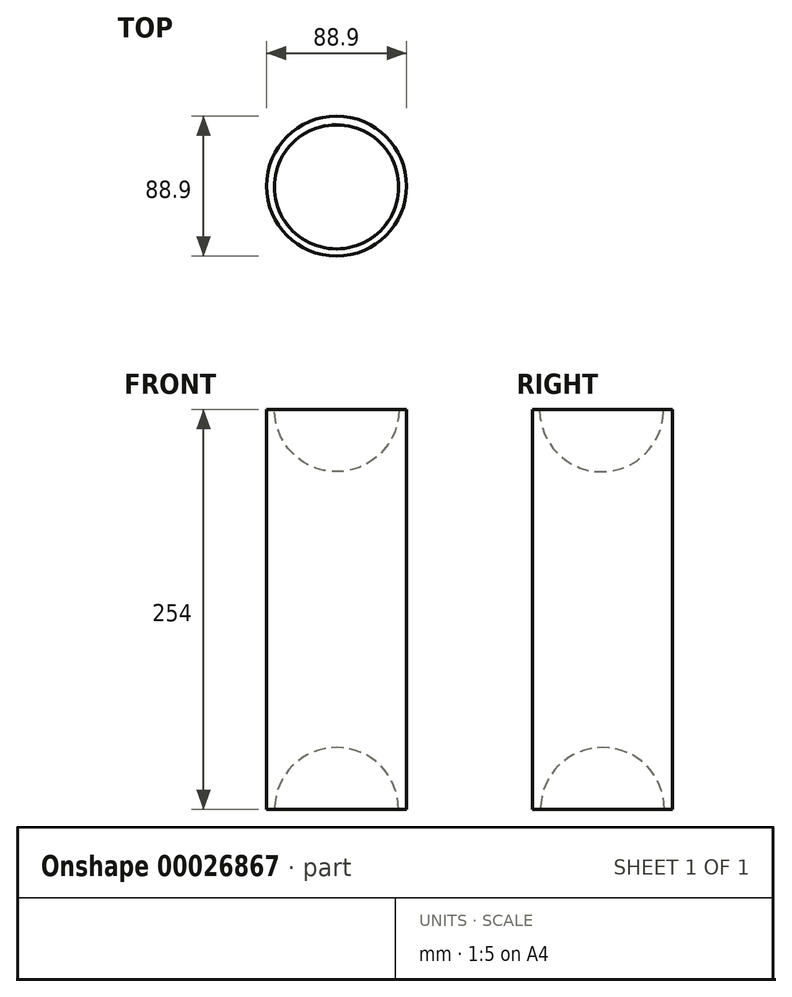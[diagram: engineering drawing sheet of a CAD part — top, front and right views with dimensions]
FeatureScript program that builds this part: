
annotation { "Feature Type Name" : "Feature", "Feature Type Description" : "" }
export const myFeature = defineFeature(function(context is Context, id is Id, definition is map)
    precondition{}
    {
        {
            var Q0;
            Q0=qCreatedBy(makeId("Top.planeOp"),FACE);
            var sketch = newSketch(context, id + "F0", { "sketchPlane" : qUnion([Q0])});
            skCircle(sketch, "E0", {"center": v(0, 0) * mm, "radius": 44.45 * mm});
            skSolve(sketch);
        }
        {
            var Q0;
            Q0=makeQuery(id+"F0.imprint","IMPRINT",FACE,{"disambiguationData":[TD([[makeQuery(id+"F0.imprint","IMPRINT",EDGE,{"derivedFrom":sQuery(id+"F0.wireOp",EDGE,"E0")}),1.0]])]});
            extrude(context, id + "F1", {"entities" : qUnion([Q0]), "depth" : 254 * mm});
        }
        {
            var Q0;
            Q0=makeQuery(id+"F1.opExtrude","CAP_FACE",FACE,{"disambiguationData":[OSD([sQuery(id+"F0.wireOp",EDGE,"E0")])],"isStart":false});
            var sketch = newSketch(context, id + "F2", { "sketchPlane" : qUnion([Q0])});
            skArc(sketch, "E1", {"start": v(0, -39.88) * mm, "mid": v(39.52, -0.5) * mm, "end": v(0, 38.86) * mm});
            skLineSegment(sketch, "E2", {"start": v(0, 38.86) * mm, "end": v(0, -39.88) * mm});
            skSolve(sketch);
        }
        {
            var Q0;
            Q0=makeQuery(id+"F2.imprint","IMPRINT",FACE,{"disambiguationData":[TD([[makeQuery(id+"F2.imprint","IMPRINT",EDGE,{"derivedFrom":sQuery(id+"F2.wireOp",EDGE,"E1")}),1.0]])]});
            var Q1;
            Q1=sQuery(id+"F2.wireOp",EDGE,"E2");
            revolve(context, id + "F3", {"operationType" : NewBodyOperationType.REMOVE, "entities" : qUnion([Q0]), "axis" : qUnion([Q1]), "revolveType" : RevolveType.ONE_DIRECTION, "oppositeDirection" : true, "angle" : 180 * degree});
        }
        {
            var Q0;
            Q0=makeQuery(id+"F1.opExtrude","CAP_FACE",FACE,{"disambiguationData":[OSD([sQuery(id+"F0.wireOp",EDGE,"E0")])],"isStart":true});
            var sketch = newSketch(context, id + "F4", { "sketchPlane" : qUnion([Q0])});
            skArc(sketch, "E3", {"start": v(39.37, 0) * mm, "mid": v(0, 39.37) * mm, "end": v(-39.37, 0) * mm});
            skLineSegment(sketch, "E4", {"start": v(39.37, 0) * mm, "end": v(-39.37, 0) * mm});
            skSolve(sketch);
        }
        {
            var Q0;
            Q0=makeQuery(id+"F4.imprint","IMPRINT",FACE,{"disambiguationData":[TD([[makeQuery(id+"F4.imprint","IMPRINT",EDGE,{"derivedFrom":sQuery(id+"F4.wireOp",EDGE,"E3")}),1.0]])]});
            var Q1;
            Q1=sQuery(id+"F4.wireOp",EDGE,"E4");
            revolve(context, id + "F5", {"operationType" : NewBodyOperationType.REMOVE, "entities" : qUnion([Q0]), "axis" : qUnion([Q1]), "revolveType" : RevolveType.ONE_DIRECTION, "angle" : 180 * degree});
        }
    });
